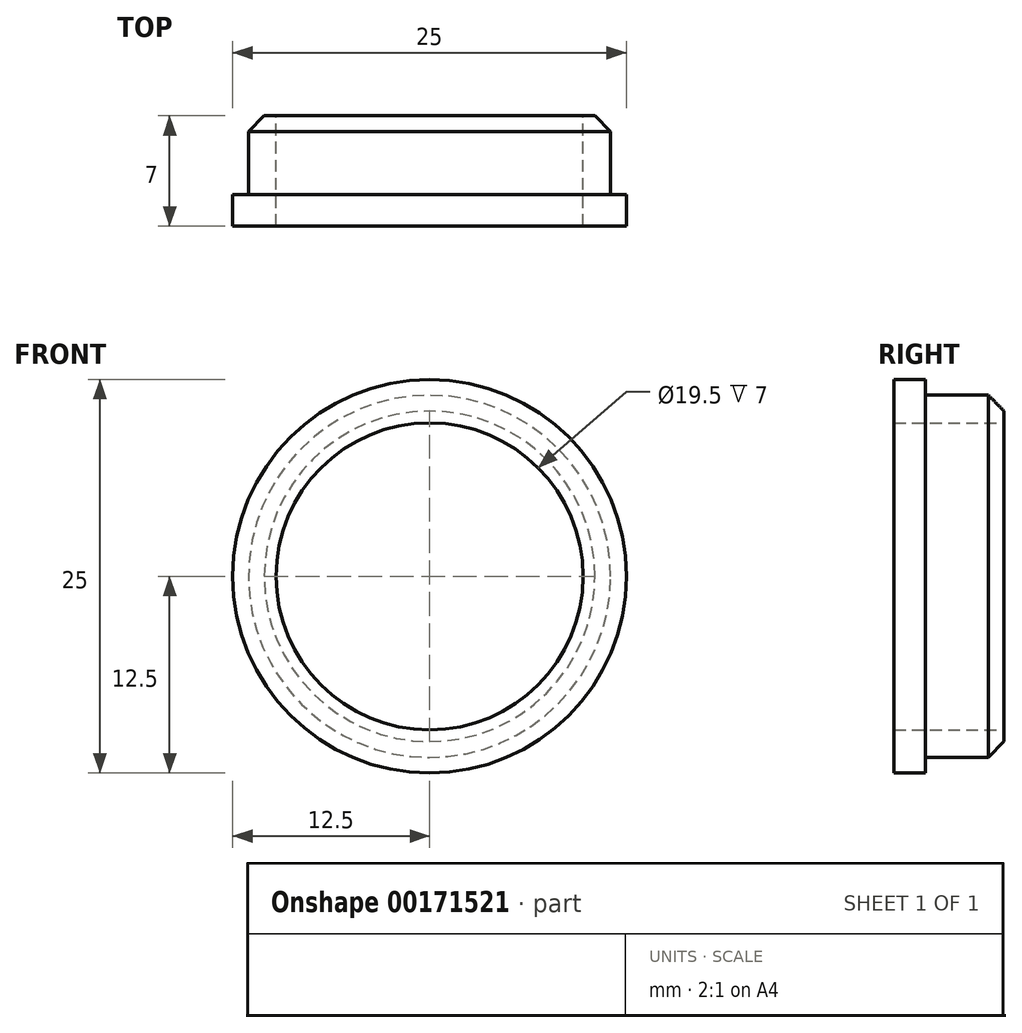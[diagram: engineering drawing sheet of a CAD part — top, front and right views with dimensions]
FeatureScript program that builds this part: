
annotation { "Feature Type Name" : "Feature", "Feature Type Description" : "" }
export const myFeature = defineFeature(function(context is Context, id is Id, definition is map)
    precondition{}
    {
        {
            var Q0;
            Q0=qCreatedBy(makeId("Right.planeOp"),FACE);
            var sketch = newSketch(context, id + "F0", { "sketchPlane" : qUnion([Q0])});
            skLineSegment(sketch, "E0", {"start": v(11.47, 0) * mm, "end": v(0, 0) * mm, "construction": true});
            skLineSegment(sketch, "E1", {"start": v(0, 0) * mm, "end": v(0, 0) * mm});
            skLineSegment(sketch, "E2", {"start": v(0, 0) * mm, "end": v(0, 9.75) * mm});
            skLineSegment(sketch, "E3", {"start": v(7, 9.75) * mm, "end": v(0, 9.75) * mm});
            skLineSegment(sketch, "E4", {"start": v(7, 9.75) * mm, "end": v(7, 11.5) * mm});
            skLineSegment(sketch, "E5", {"start": v(2, 11.5) * mm, "end": v(7, 11.5) * mm});
            skLineSegment(sketch, "E6", {"start": v(2, 11.5) * mm, "end": v(2, 12.5) * mm});
            skLineSegment(sketch, "E7", {"start": v(0, 12.5) * mm, "end": v(2, 12.5) * mm});
            skLineSegment(sketch, "E8", {"start": v(0, 12.5) * mm, "end": v(0, 0) * mm});
            skSolve(sketch);
        }
        {
            var Q0;
            {var subQ0=sQuery(id+"F0.wireOp",EDGE,"E3");Q0=makeQuery(id+"F0.imprint","IMPRINT",FACE,{"disambiguationData":[TD([[makeQuery(id+"F0.imprint","IMPRINT",EDGE,{"derivedFrom":subQ0}),-1.0]])]});}
            var Q1;
            Q1=sQuery(id+"F0.wireOp",EDGE,"E0");
            revolve(context, id + "F1", {"entities" : qUnion([Q0]), "axis" : qUnion([Q1]), "revolveType" : RevolveType.FULL});
        }
        {
            var Q0;
            Q0=makeQuery(id+"F1.opRevolve","SWEPT_EDGE",EDGE,{"disambiguationData":[OSD([sQuery(id+"F0.wireOp",EDGE,"E4"),sQuery(id+"F0.wireOp",EDGE,"E5")])]});
            chamfer(context, id + "F2", {"entities" : qUnion([Q0]), "width" : 1 * mm, "tangentPropagation" : true});
        }
    });
